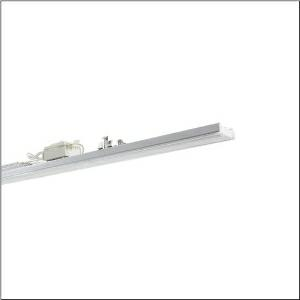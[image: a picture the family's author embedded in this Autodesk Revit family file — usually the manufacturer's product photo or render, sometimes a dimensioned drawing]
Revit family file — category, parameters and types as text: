
# Revit family: licross_r__11_recessed_ho_51tl12dv4m2m3c_86c7
name_source: partatom
category: Lighting Fixtures
units: mm (PartAtom-declared; Revit-internal decimal feet)

## family parameters
Cut with Voids When Loaded = No
Host = Face
Light Source = No
Part Type = Normal
Room Calculation Point = No
Round Connector Dimension = Use Diameter
Shared = No

## types (1)
- --- (1 x LED, 1010 lm, 5.9 W, 4000K)
    Apparent Load = 6 VA
    CIE Flux Codes = 66 91 98 100 100
    Color Rendering = 80
    Color Temperature = 4000K
    Default Elevation = 1800 mm
    Description = Licross® 11 Recessed HO, luminaire insert, of sheet steel, coil coated, white, length: 2.250mm, width: 66mm, height: 67mm, LED rated luminous flux: 27.150lm, light colour: 840, control gear: DALI 2 (for two DALI lines), with plug, 6-pole, with phase selection, for trunking rail, 14-core, mains connection: 220..240V, AC, 50/60Hz, rated input power: 154W, for trunking rail, 14-core, halogen-free wiring, for emergency light function, converter,control gear: single battery element, battery: LiFePO4, 9Ah, primary optical cover: cover, of PMMA, light emission: direct distribution, primary light characteristic: symmetric, protection rating (complete): IP40, insulation class (complete): insulation class I (protective earthing), certification: CE, UKCA, protection symbol: D if used in an environment without relevant dust loads with corresponding accessories, impact resistance: IK06, permissible ambient temperature for indoor applications: +5..+35°C, standard: EN 60598-2-22, LABS conformity tested according to VDMA 24364:2018-05, reducing of maximum allowable ambient temperature of 5°C with ceiling mounting, corresponds to IFS (International Featured Standards) requirements for safety and quality in the food industry, packaging unit: 1 piece
    Height = 58 mm
    Lamp = 1 x LED
    Lamp Light Flux = 1010 lm
    Lamp Power = 5.9 W
    Lamp count = 1
    Length = 2250 mm
    Luminous efficacy = 171 lm/W
    Manufacturer = Siteco
    ModVariant = No
    Model = 51TL12DV4M2M3C
    Mounting Place = Ceiling
    Mounting Type = Pendant
    Number of Poles = 1
    OnlyDefault = Yes
    Power Factor = 1
    Product Name = Licross® 11 Recessed HO
    Product group = luminaire insert
    ProductGroupID = 902
    Protection Class = Protection class I
    Protection Degree = IP 40
    RLX_Detail_Level = 1
    RLX_Emergency_Light_Flux = 0 lm
    RLX_Emergency_Type = 0
    RLX_Emergency_Type_DB = No
    RlxData = <blob elided: 29953 chars, md5=c5547856>
    Socket = socket
    Standby Power = 0 W
    System Light Flux = 1010 lm
    System Power = 6 W
    Type Comments = : emergency light operation: 3 h
    Type Image = l_1296930.jpg
    URL = http://relux.com
    VarID = @adj_084768
    Voltage = 0 V
    Weight = 0.00 kg
    Width = 66 mm

## geometry (parser evidence)
native form markers: Blend x4, Sweep x10
no freeform markers — native parametric forms only
